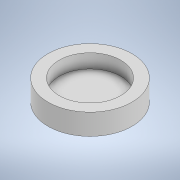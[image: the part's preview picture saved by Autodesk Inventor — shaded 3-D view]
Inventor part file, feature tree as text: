
AUTODESK INVENTOR PART (.ipt)
format: ipt  version: 2020 (Build 240168000, 168)  size: 103,936 bytes
history: native  units: in
note: dims shown in document units (in); Inventor stores cm internally (conversion verified against a paired STEP export)
features: extrude x2, sketch x2
ambient origin geometry x8: Origin, YZ Plane, XZ Plane, XY Plane, X Axis, Y Axis, Z Axis, Center Point
bodies: Solid1 (feature_tree)
feature tree (4):
  extrude  "Extrusion1"  Depth=0.375in TaperAngle=0.0deg
  extrude  "Extrusion2"  Depth=0.25in TaperAngle=0.0deg
  sketch  "Sketch1"  dims[d0=1.5in d1=0.375in d2=0.0in]
  sketch  "Sketch2"  dims[d3=1.1in d4=0.25in d5=0.0in]
